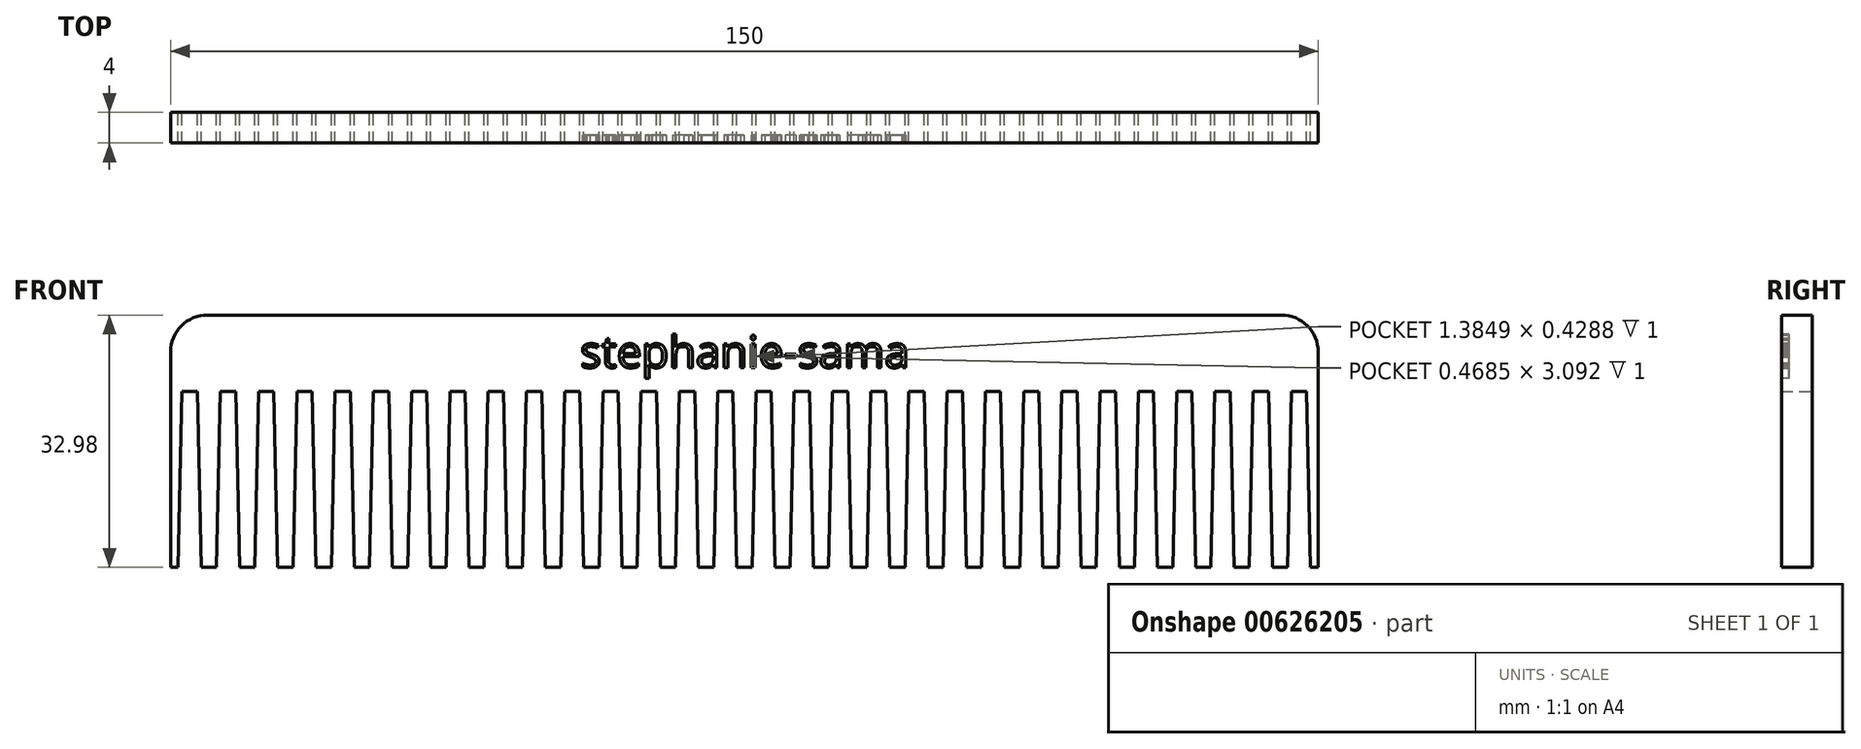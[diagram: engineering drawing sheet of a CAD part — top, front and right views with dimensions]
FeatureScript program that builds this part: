
annotation { "Feature Type Name" : "Feature", "Feature Type Description" : "" }
export const myFeature = defineFeature(function(context is Context, id is Id, definition is map)
    precondition{}
    {
        {
            var Q0;
            Q0=qCreatedBy(makeId("Front.planeOp"),FACE);
            var sketch = newSketch(context, id + "F0", { "sketchPlane" : qUnion([Q0])});
            skLineSegment(sketch, "E0.bottom", {"start": v(0, 0) * mm, "end": v(1, 0) * mm});
            skLineSegment(sketch, "E0.top", {"start": v(0, 32.98) * mm, "end": v(75, 32.98) * mm});
            skLineSegment(sketch, "E0.left", {"start": v(0, 0) * mm, "end": v(0, 32.98) * mm});
            skLineSegment(sketch, "E0.right", {"start": v(75, 0) * mm, "end": v(75, 32.98) * mm});
            skLineSegment(sketch, "E1", {"start": v(1, 0) * mm, "end": v(1.5, 23) * mm});
            skLineSegment(sketch, "E2", {"start": v(3.5, 23) * mm, "end": v(4, 0) * mm});
            skLineSegment(sketch, "E3", {"start": v(1.5, 23) * mm, "end": v(3.5, 23) * mm});
            skLineSegment(sketch, "E4", {"start": v(2.5, 23) * mm, "end": v(2.5, -1.32) * mm, "construction": true});
            skLineSegment(sketch, "E5.1.0.0", {"start": v(6, 0) * mm, "end": v(6.5, 23) * mm});
            skLineSegment(sketch, "E5.1.0.1", {"start": v(8.5, 23) * mm, "end": v(9, 0) * mm});
            skLineSegment(sketch, "E5.1.0.2", {"start": v(6.5, 23) * mm, "end": v(8.5, 23) * mm});
            skLineSegment(sketch, "E5.2.0.0", {"start": v(11, 0) * mm, "end": v(11.5, 23) * mm});
            skLineSegment(sketch, "E5.2.0.1", {"start": v(13.5, 23) * mm, "end": v(14, 0) * mm});
            skLineSegment(sketch, "E5.2.0.2", {"start": v(11.5, 23) * mm, "end": v(13.5, 23) * mm});
            skLineSegment(sketch, "E5.3.0.0", {"start": v(16, 0) * mm, "end": v(16.5, 23) * mm});
            skLineSegment(sketch, "E5.3.0.1", {"start": v(18.5, 23) * mm, "end": v(19, 0) * mm});
            skLineSegment(sketch, "E5.3.0.2", {"start": v(16.5, 23) * mm, "end": v(18.5, 23) * mm});
            skLineSegment(sketch, "E5.4.0.0", {"start": v(21, 0) * mm, "end": v(21.5, 23) * mm});
            skLineSegment(sketch, "E5.4.0.1", {"start": v(23.5, 23) * mm, "end": v(24, 0) * mm});
            skLineSegment(sketch, "E5.4.0.2", {"start": v(21.5, 23) * mm, "end": v(23.5, 23) * mm});
            skLineSegment(sketch, "E5.5.0.0", {"start": v(26, 0) * mm, "end": v(26.5, 23) * mm});
            skLineSegment(sketch, "E5.5.0.1", {"start": v(28.5, 23) * mm, "end": v(29, 0) * mm});
            skLineSegment(sketch, "E5.5.0.2", {"start": v(26.5, 23) * mm, "end": v(28.5, 23) * mm});
            skLineSegment(sketch, "E5.6.0.0", {"start": v(31, 0) * mm, "end": v(31.5, 23) * mm});
            skLineSegment(sketch, "E5.6.0.1", {"start": v(33.5, 23) * mm, "end": v(34, 0) * mm});
            skLineSegment(sketch, "E5.6.0.2", {"start": v(31.5, 23) * mm, "end": v(33.5, 23) * mm});
            skLineSegment(sketch, "E5.7.0.0", {"start": v(36, 0) * mm, "end": v(36.5, 23) * mm});
            skLineSegment(sketch, "E5.7.0.1", {"start": v(38.5, 23) * mm, "end": v(39, 0) * mm});
            skLineSegment(sketch, "E5.7.0.2", {"start": v(36.5, 23) * mm, "end": v(38.5, 23) * mm});
            skLineSegment(sketch, "E5.8.0.0", {"start": v(41, 0) * mm, "end": v(41.5, 23) * mm});
            skLineSegment(sketch, "E5.8.0.1", {"start": v(43.5, 23) * mm, "end": v(44, 0) * mm});
            skLineSegment(sketch, "E5.8.0.2", {"start": v(41.5, 23) * mm, "end": v(43.5, 23) * mm});
            skLineSegment(sketch, "E5.9.0.0", {"start": v(46, 0) * mm, "end": v(46.5, 23) * mm});
            skLineSegment(sketch, "E5.9.0.1", {"start": v(48.5, 23) * mm, "end": v(49, 0) * mm});
            skLineSegment(sketch, "E5.9.0.2", {"start": v(46.5, 23) * mm, "end": v(48.5, 23) * mm});
            skLineSegment(sketch, "E5.10.0.0", {"start": v(51, 0) * mm, "end": v(51.5, 23) * mm});
            skLineSegment(sketch, "E5.10.0.1", {"start": v(53.5, 23) * mm, "end": v(54, 0) * mm});
            skLineSegment(sketch, "E5.10.0.2", {"start": v(51.5, 23) * mm, "end": v(53.5, 23) * mm});
            skLineSegment(sketch, "E5.11.0.0", {"start": v(56, 0) * mm, "end": v(56.5, 23) * mm});
            skLineSegment(sketch, "E5.11.0.1", {"start": v(58.5, 23) * mm, "end": v(59, 0) * mm});
            skLineSegment(sketch, "E5.11.0.2", {"start": v(56.5, 23) * mm, "end": v(58.5, 23) * mm});
            skLineSegment(sketch, "E5.12.0.0", {"start": v(61, 0) * mm, "end": v(61.5, 23) * mm});
            skLineSegment(sketch, "E5.12.0.1", {"start": v(63.5, 23) * mm, "end": v(64, 0) * mm});
            skLineSegment(sketch, "E5.12.0.2", {"start": v(61.5, 23) * mm, "end": v(63.5, 23) * mm});
            skLineSegment(sketch, "E5.13.0.0", {"start": v(66, 0) * mm, "end": v(66.5, 23) * mm});
            skLineSegment(sketch, "E5.13.0.1", {"start": v(68.5, 23) * mm, "end": v(69, 0) * mm});
            skLineSegment(sketch, "E5.13.0.2", {"start": v(66.5, 23) * mm, "end": v(68.5, 23) * mm});
            skLineSegment(sketch, "E5.14.0.0", {"start": v(71, 0) * mm, "end": v(71.5, 23) * mm});
            skLineSegment(sketch, "E5.14.0.1", {"start": v(73.5, 23) * mm, "end": v(74, 0) * mm});
            skLineSegment(sketch, "E5.14.0.2", {"start": v(71.5, 23) * mm, "end": v(73.5, 23) * mm});
            skLineSegment(sketch, "E5.direction1", {"start": v(4, 0) * mm, "end": v(6, 0) * mm, "construction": true});
            skLineSegment(sketch, "E6.trimOffspring", {"start": v(19, 0) * mm, "end": v(21, 0) * mm});
            skLineSegment(sketch, "E7.trimOffspring", {"start": v(24, 0) * mm, "end": v(26, 0) * mm});
            skLineSegment(sketch, "E8.trimOffspring", {"start": v(29, 0) * mm, "end": v(31, 0) * mm});
            skLineSegment(sketch, "E9.trimOffspring", {"start": v(34, 0) * mm, "end": v(36, 0) * mm});
            skLineSegment(sketch, "E10.trimOffspring", {"start": v(39, 0) * mm, "end": v(41, 0) * mm});
            skLineSegment(sketch, "E11.trimOffspring", {"start": v(44, 0) * mm, "end": v(46, 0) * mm});
            skLineSegment(sketch, "E12.trimOffspring", {"start": v(49, 0) * mm, "end": v(51, 0) * mm});
            skLineSegment(sketch, "E13.trimOffspring", {"start": v(54, 0) * mm, "end": v(56, 0) * mm});
            skLineSegment(sketch, "E14.trimOffspring", {"start": v(59, 0) * mm, "end": v(61, 0) * mm});
            skLineSegment(sketch, "E15.trimOffspring", {"start": v(64, 0) * mm, "end": v(66, 0) * mm});
            skLineSegment(sketch, "E16.trimOffspring", {"start": v(69, 0) * mm, "end": v(71, 0) * mm});
            skLineSegment(sketch, "E17.trimOffspring", {"start": v(74, 0) * mm, "end": v(75, 0) * mm});
            skLineSegment(sketch, "E18.trimOffspring", {"start": v(14, 0) * mm, "end": v(16, 0) * mm});
            skLineSegment(sketch, "E19.trimOffspring", {"start": v(9, 0) * mm, "end": v(11, 0) * mm});
            skLineSegment(sketch, "E20.trimOffspring", {"start": v(2.5, 0) * mm, "end": v(6, 0) * mm});
            skSolve(sketch);
        }
        {
            var Q0;
            Q0=makeQuery(id+"F0.imprint","IMPRINT",FACE,{"disambiguationData":[TD([[makeQuery(id+"F0.imprint","IMPRINT",EDGE,{"derivedFrom":sQuery(id+"F0.wireOp",EDGE,"E0.bottom")}),1.0]])]});
            extrude(context, id + "F1", {"entities" : qUnion([Q0]), "depth" : 4 * mm, "offsetDistance" : 25 * mm});
        }
        {
            var Q0;
            Q0=makeQuery(id+"F1.opExtrude","SWEPT_EDGE",EDGE,{"disambiguationData":[OSD([sQuery(id+"F0.wireOp",EDGE,"E0.top"),sQuery(id+"F0.wireOp",EDGE,"E0.right")])]});
            fillet(context, id + "F2", {"entities" : qUnion([Q0]), "radius" : 4.83 * mm, "tangentPropagation" : true, "allowEdgeOverflow" : false});
        }
        {
            var Q0;
            Q0=makeQuery(id+"F1.opExtrude","SWEPT_BODY",BODY,{"disambiguationData":[OSD([sQuery(id+"F0.wireOp",EDGE,"E0.bottom"),sQuery(id+"F0.wireOp",EDGE,"E0.top"),sQuery(id+"F0.wireOp",EDGE,"E0.left"),sQuery(id+"F0.wireOp",EDGE,"E0.right"),sQuery(id+"F0.wireOp",EDGE,"E1"),sQuery(id+"F0.wireOp",EDGE,"E2"),sQuery(id+"F0.wireOp",EDGE,"E3"),sQuery(id+"F0.wireOp",EDGE,"E5.1.0.0"),sQuery(id+"F0.wireOp",EDGE,"E5.1.0.1"),sQuery(id+"F0.wireOp",EDGE,"E5.1.0.2"),sQuery(id+"F0.wireOp",EDGE,"E5.2.0.0"),sQuery(id+"F0.wireOp",EDGE,"E5.2.0.1"),sQuery(id+"F0.wireOp",EDGE,"E5.2.0.2"),sQuery(id+"F0.wireOp",EDGE,"E5.3.0.0"),sQuery(id+"F0.wireOp",EDGE,"E5.3.0.1"),sQuery(id+"F0.wireOp",EDGE,"E5.3.0.2"),sQuery(id+"F0.wireOp",EDGE,"E5.4.0.0"),sQuery(id+"F0.wireOp",EDGE,"E5.4.0.1"),sQuery(id+"F0.wireOp",EDGE,"E5.4.0.2"),sQuery(id+"F0.wireOp",EDGE,"E5.5.0.0"),sQuery(id+"F0.wireOp",EDGE,"E5.5.0.1"),sQuery(id+"F0.wireOp",EDGE,"E5.5.0.2"),sQuery(id+"F0.wireOp",EDGE,"E5.6.0.0"),sQuery(id+"F0.wireOp",EDGE,"E5.6.0.1"),sQuery(id+"F0.wireOp",EDGE,"E5.6.0.2"),sQuery(id+"F0.wireOp",EDGE,"E5.7.0.0"),sQuery(id+"F0.wireOp",EDGE,"E5.7.0.1"),sQuery(id+"F0.wireOp",EDGE,"E5.7.0.2"),sQuery(id+"F0.wireOp",EDGE,"E5.8.0.0"),sQuery(id+"F0.wireOp",EDGE,"E5.8.0.1"),sQuery(id+"F0.wireOp",EDGE,"E5.8.0.2"),sQuery(id+"F0.wireOp",EDGE,"E5.9.0.0"),sQuery(id+"F0.wireOp",EDGE,"E5.9.0.1"),sQuery(id+"F0.wireOp",EDGE,"E5.9.0.2"),sQuery(id+"F0.wireOp",EDGE,"E5.10.0.0"),sQuery(id+"F0.wireOp",EDGE,"E5.10.0.1"),sQuery(id+"F0.wireOp",EDGE,"E5.10.0.2"),sQuery(id+"F0.wireOp",EDGE,"E5.11.0.0"),sQuery(id+"F0.wireOp",EDGE,"E5.11.0.1"),sQuery(id+"F0.wireOp",EDGE,"E5.11.0.2"),sQuery(id+"F0.wireOp",EDGE,"E5.12.0.0"),sQuery(id+"F0.wireOp",EDGE,"E5.12.0.1"),sQuery(id+"F0.wireOp",EDGE,"E5.12.0.2"),sQuery(id+"F0.wireOp",EDGE,"E5.13.0.0"),sQuery(id+"F0.wireOp",EDGE,"E5.13.0.1"),sQuery(id+"F0.wireOp",EDGE,"E5.13.0.2"),sQuery(id+"F0.wireOp",EDGE,"E5.14.0.0"),sQuery(id+"F0.wireOp",EDGE,"E5.14.0.1"),sQuery(id+"F0.wireOp",EDGE,"E5.14.0.2"),sQuery(id+"F0.wireOp",EDGE,"E6.trimOffspring"),sQuery(id+"F0.wireOp",EDGE,"E7.trimOffspring"),sQuery(id+"F0.wireOp",EDGE,"E8.trimOffspring"),sQuery(id+"F0.wireOp",EDGE,"E9.trimOffspring"),sQuery(id+"F0.wireOp",EDGE,"E10.trimOffspring"),sQuery(id+"F0.wireOp",EDGE,"E11.trimOffspring"),sQuery(id+"F0.wireOp",EDGE,"E12.trimOffspring"),sQuery(id+"F0.wireOp",EDGE,"E13.trimOffspring"),sQuery(id+"F0.wireOp",EDGE,"E14.trimOffspring"),sQuery(id+"F0.wireOp",EDGE,"E15.trimOffspring"),sQuery(id+"F0.wireOp",EDGE,"E16.trimOffspring"),sQuery(id+"F0.wireOp",EDGE,"E17.trimOffspring"),sQuery(id+"F0.wireOp",EDGE,"E18.trimOffspring"),sQuery(id+"F0.wireOp",EDGE,"E19.trimOffspring"),sQuery(id+"F0.wireOp",EDGE,"E20.trimOffspring")])]});
            var Q1;
            Q1=qCreatedBy(makeId("Right.planeOp"),FACE);
            mirror(context, id + "F3", {"operationType" : NewBodyOperationType.ADD, "entities" : qUnion([Q0]), "mirrorPlane" : qUnion([Q1])});
        }
        {
            var Q0;
            {var subQ0=makeQuery(id+"F1.opExtrude","CAP_FACE",FACE,{"disambiguationData":[OSD([sQuery(id+"F0.wireOp",EDGE,"E0.bottom"),sQuery(id+"F0.wireOp",EDGE,"E0.top"),sQuery(id+"F0.wireOp",EDGE,"E0.left"),sQuery(id+"F0.wireOp",EDGE,"E0.right"),sQuery(id+"F0.wireOp",EDGE,"E1"),sQuery(id+"F0.wireOp",EDGE,"E2"),sQuery(id+"F0.wireOp",EDGE,"E3"),sQuery(id+"F0.wireOp",EDGE,"E5.1.0.0"),sQuery(id+"F0.wireOp",EDGE,"E5.1.0.1"),sQuery(id+"F0.wireOp",EDGE,"E5.1.0.2"),sQuery(id+"F0.wireOp",EDGE,"E5.2.0.0"),sQuery(id+"F0.wireOp",EDGE,"E5.2.0.1"),sQuery(id+"F0.wireOp",EDGE,"E5.2.0.2"),sQuery(id+"F0.wireOp",EDGE,"E5.3.0.0"),sQuery(id+"F0.wireOp",EDGE,"E5.3.0.1"),sQuery(id+"F0.wireOp",EDGE,"E5.3.0.2"),sQuery(id+"F0.wireOp",EDGE,"E5.4.0.0"),sQuery(id+"F0.wireOp",EDGE,"E5.4.0.1"),sQuery(id+"F0.wireOp",EDGE,"E5.4.0.2"),sQuery(id+"F0.wireOp",EDGE,"E5.5.0.0"),sQuery(id+"F0.wireOp",EDGE,"E5.5.0.1"),sQuery(id+"F0.wireOp",EDGE,"E5.5.0.2"),sQuery(id+"F0.wireOp",EDGE,"E5.6.0.0"),sQuery(id+"F0.wireOp",EDGE,"E5.6.0.1"),sQuery(id+"F0.wireOp",EDGE,"E5.6.0.2"),sQuery(id+"F0.wireOp",EDGE,"E5.7.0.0"),sQuery(id+"F0.wireOp",EDGE,"E5.7.0.1"),sQuery(id+"F0.wireOp",EDGE,"E5.7.0.2"),sQuery(id+"F0.wireOp",EDGE,"E5.8.0.0"),sQuery(id+"F0.wireOp",EDGE,"E5.8.0.1"),sQuery(id+"F0.wireOp",EDGE,"E5.8.0.2"),sQuery(id+"F0.wireOp",EDGE,"E5.9.0.0"),sQuery(id+"F0.wireOp",EDGE,"E5.9.0.1"),sQuery(id+"F0.wireOp",EDGE,"E5.9.0.2"),sQuery(id+"F0.wireOp",EDGE,"E5.10.0.0"),sQuery(id+"F0.wireOp",EDGE,"E5.10.0.1"),sQuery(id+"F0.wireOp",EDGE,"E5.10.0.2"),sQuery(id+"F0.wireOp",EDGE,"E5.11.0.0"),sQuery(id+"F0.wireOp",EDGE,"E5.11.0.1"),sQuery(id+"F0.wireOp",EDGE,"E5.11.0.2"),sQuery(id+"F0.wireOp",EDGE,"E5.12.0.0"),sQuery(id+"F0.wireOp",EDGE,"E5.12.0.1"),sQuery(id+"F0.wireOp",EDGE,"E5.12.0.2"),sQuery(id+"F0.wireOp",EDGE,"E5.13.0.0"),sQuery(id+"F0.wireOp",EDGE,"E5.13.0.1"),sQuery(id+"F0.wireOp",EDGE,"E5.13.0.2"),sQuery(id+"F0.wireOp",EDGE,"E5.14.0.0"),sQuery(id+"F0.wireOp",EDGE,"E5.14.0.1"),sQuery(id+"F0.wireOp",EDGE,"E5.14.0.2"),sQuery(id+"F0.wireOp",EDGE,"E6.trimOffspring"),sQuery(id+"F0.wireOp",EDGE,"E7.trimOffspring"),sQuery(id+"F0.wireOp",EDGE,"E8.trimOffspring"),sQuery(id+"F0.wireOp",EDGE,"E9.trimOffspring"),sQuery(id+"F0.wireOp",EDGE,"E10.trimOffspring"),sQuery(id+"F0.wireOp",EDGE,"E11.trimOffspring"),sQuery(id+"F0.wireOp",EDGE,"E12.trimOffspring"),sQuery(id+"F0.wireOp",EDGE,"E13.trimOffspring"),sQuery(id+"F0.wireOp",EDGE,"E14.trimOffspring"),sQuery(id+"F0.wireOp",EDGE,"E15.trimOffspring"),sQuery(id+"F0.wireOp",EDGE,"E16.trimOffspring"),sQuery(id+"F0.wireOp",EDGE,"E17.trimOffspring"),sQuery(id+"F0.wireOp",EDGE,"E18.trimOffspring"),sQuery(id+"F0.wireOp",EDGE,"E19.trimOffspring"),sQuery(id+"F0.wireOp",EDGE,"E20.trimOffspring")])],"isStart":false});Q0=makeQuery(id+"F3.boolean.opBoolean","MERGE",FACE,{"derivedFrom":[subQ0,makeQuery(id+"F3.opPattern","COPY",FACE,{"derivedFrom":subQ0,"instanceName":"1"})]});}
            var sketch = newSketch(context, id + "F4", { "sketchPlane" : qUnion([Q0])});
            skText(sketch, "E21", { "text": "stephanie-sama", "fontName": "OpenSans-Regular.ttf"});
            const initialGuessF4  = {"E21": [-0.02147, 0.0261, 1, 0, 0.00416]};
            skSetInitialGuess(sketch, initialGuessF4);
            skSolve(sketch);
        }
        {
            var Q0;
            Q0 = qSketchRegion(id + "F4", true);
            extrude(context, id + "F5", {"entities" : qUnion([Q0]), "operationType" : NewBodyOperationType.REMOVE, "oppositeDirection" : true, "depth" : 1 * mm, "offsetDistance" : 25 * mm});
        }
    });
